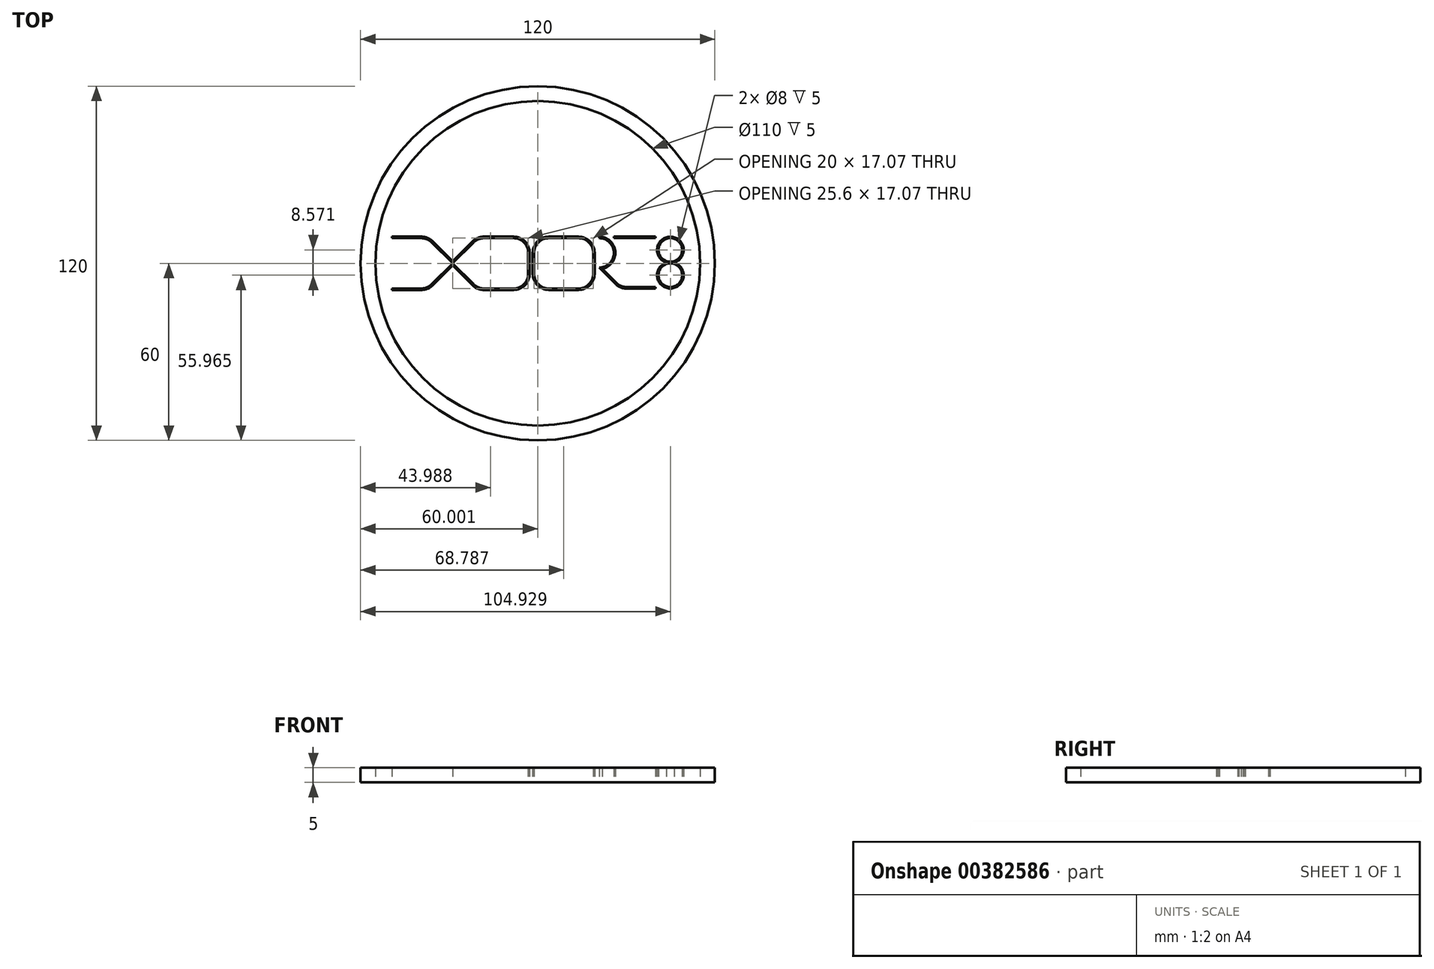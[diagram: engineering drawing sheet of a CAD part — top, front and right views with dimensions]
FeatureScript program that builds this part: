
annotation { "Feature Type Name" : "Feature", "Feature Type Description" : "" }
export const myFeature = defineFeature(function(context is Context, id is Id, definition is map)
    precondition{}
    {
        {
            var Q0;
            Q0=qCreatedBy(makeId("Top.planeOp"),FACE);
            var sketch = newSketch(context, id + "F0", { "sketchPlane" : qUnion([Q0])});
            skLineSegment(sketch, "E0", {"start": v(-7.07, 7.07) * mm, "end": v(0, 0) * mm});
            skLineSegment(sketch, "E1", {"start": v(-7.07, -7.07) * mm, "end": v(0, 0) * mm});
            skLineSegment(sketch, "E2", {"start": v(0, 0) * mm, "end": v(7.07, 7.07) * mm});
            skLineSegment(sketch, "E3", {"start": v(0, 0) * mm, "end": v(7.07, -7.07) * mm});
            skArc(sketch, "E4", {"start": v(-7.07, 7.07) * mm, "mid": v(-8.7, 8.15) * mm, "end": v(-10.6, 8.54) * mm});
            skLineSegment(sketch, "E5", {"start": v(-10.6, 8.54) * mm, "end": v(-20.6, 8.54) * mm});
            skArc(sketch, "E6", {"start": v(-10.6, -8.54) * mm, "mid": v(-8.7, -8.15) * mm, "end": v(-7.07, -7.07) * mm});
            skLineSegment(sketch, "E7", {"start": v(-10.6, -8.54) * mm, "end": v(-20.6, -8.54) * mm});
            skArc(sketch, "E8", {"start": v(10.6, 8.54) * mm, "mid": v(8.7, 8.15) * mm, "end": v(7.07, 7.07) * mm});
            skLineSegment(sketch, "E9", {"start": v(10.6, 8.54) * mm, "end": v(20.6, 8.54) * mm});
            skArc(sketch, "E10", {"start": v(7.07, -7.07) * mm, "mid": v(8.7, -8.15) * mm, "end": v(10.6, -8.54) * mm});
            skLineSegment(sketch, "E11", {"start": v(10.6, -8.54) * mm, "end": v(20.6, -8.54) * mm});
            skArc(sketch, "E12", {"start": v(25.6, 3.54) * mm, "mid": v(24.14, 7.07) * mm, "end": v(20.6, 8.54) * mm});
            skArc(sketch, "E13", {"start": v(20.6, -8.54) * mm, "mid": v(24.14, -7.07) * mm, "end": v(25.6, -3.54) * mm});
            skLineSegment(sketch, "E14", {"start": v(25.6, 3.54) * mm, "end": v(25.6, -3.54) * mm});
            skLineSegment(sketch, "E15", {"start": v(27.6, 3.54) * mm, "end": v(27.6, -3.54) * mm});
            skArc(sketch, "E16", {"start": v(32.6, 8.54) * mm, "mid": v(29.07, 7.07) * mm, "end": v(27.6, 3.54) * mm});
            skArc(sketch, "E17", {"start": v(27.6, -3.54) * mm, "mid": v(29.07, -7.07) * mm, "end": v(32.6, -8.54) * mm});
            skLineSegment(sketch, "E18", {"start": v(32.6, 8.54) * mm, "end": v(42.6, 8.54) * mm});
            skLineSegment(sketch, "E19", {"start": v(32.6, -8.54) * mm, "end": v(42.6, -8.54) * mm});
            skArc(sketch, "E20", {"start": v(47.6, 3.54) * mm, "mid": v(46.14, 7.07) * mm, "end": v(42.6, 8.54) * mm});
            skArc(sketch, "E21", {"start": v(42.6, -8.54) * mm, "mid": v(46.14, -7.07) * mm, "end": v(47.6, -3.54) * mm});
            skLineSegment(sketch, "E22", {"start": v(47.6, -3.54) * mm, "end": v(47.6, 3.54) * mm});
            skArc(sketch, "E23", {"start": v(49.6, -1.46) * mm, "mid": v(54.6, 3.54) * mm, "end": v(49.6, 8.54) * mm});
            skLineSegment(sketch, "E24", {"start": v(49.6, -1.46) * mm, "end": v(55.21, -7.07) * mm});
            skArc(sketch, "E25", {"start": v(55.21, -7.07) * mm, "mid": v(56.84, -8.15) * mm, "end": v(58.75, -8.54) * mm});
            skLineSegment(sketch, "E26", {"start": v(58.75, -8.54) * mm, "end": v(68.75, -8.54) * mm});
            skLineSegment(sketch, "E27", {"start": v(54.6, 8.54) * mm, "end": v(68.75, 8.54) * mm});
            skCircle(sketch, "E28", {"center": v(73.75, 4.54) * mm, "radius": 4 * mm});
            skCircle(sketch, "E29", {"center": v(73.75, -4.04) * mm, "radius": 4.5 * mm});
            skLineSegment(sketch, "E30.0", {"start": v(-10.6, 9.04) * mm, "end": v(-20.6, 9.04) * mm});
            skArc(sketch, "E30.1", {"start": v(-6.72, 7.42) * mm, "mid": v(-8.5, 8.62) * mm, "end": v(-10.6, 9.04) * mm});
            skLineSegment(sketch, "E30.2", {"start": v(-6.72, 7.42) * mm, "end": v(0, 0.7) * mm});
            skArc(sketch, "E30.3", {"start": v(26.1, 3.54) * mm, "mid": v(24.5, 7.42) * mm, "end": v(20.6, 9.04) * mm});
            skLineSegment(sketch, "E30.4", {"start": v(10.6, 9.04) * mm, "end": v(20.6, 9.04) * mm});
            skArc(sketch, "E30.5", {"start": v(10.6, 9.04) * mm, "mid": v(8.5, 8.62) * mm, "end": v(6.72, 7.42) * mm});
            skLineSegment(sketch, "E30.6", {"start": v(0, 0.7) * mm, "end": v(6.72, 7.42) * mm});
            skLineSegment(sketch, "E31.0", {"start": v(26.1, 3.54) * mm, "end": v(26.1, -3.54) * mm});
            skArc(sketch, "E32.0", {"start": v(20.6, -9.04) * mm, "mid": v(24.5, -7.42) * mm, "end": v(26.1, -3.54) * mm});
            skLineSegment(sketch, "E32.1", {"start": v(10.6, -9.04) * mm, "end": v(20.6, -9.04) * mm});
            skArc(sketch, "E32.2", {"start": v(6.72, -7.42) * mm, "mid": v(8.5, -8.62) * mm, "end": v(10.6, -9.04) * mm});
            skLineSegment(sketch, "E32.3", {"start": v(-10.6, -9.04) * mm, "end": v(-20.6, -9.04) * mm});
            skArc(sketch, "E32.4", {"start": v(-10.6, -9.04) * mm, "mid": v(-8.5, -8.62) * mm, "end": v(-6.72, -7.42) * mm});
            skLineSegment(sketch, "E32.5", {"start": v(-6.72, -7.42) * mm, "end": v(0, -0.7) * mm});
            skLineSegment(sketch, "E32.6", {"start": v(0, -0.7) * mm, "end": v(6.72, -7.42) * mm});
            skLineSegment(sketch, "E33.0", {"start": v(32.6, 9.04) * mm, "end": v(42.6, 9.04) * mm});
            skArc(sketch, "E33.1", {"start": v(48.1, 3.54) * mm, "mid": v(46.5, 7.42) * mm, "end": v(42.6, 9.04) * mm});
            skArc(sketch, "E33.2", {"start": v(32.6, 9.04) * mm, "mid": v(28.72, 7.42) * mm, "end": v(27.1, 3.54) * mm});
            skLineSegment(sketch, "E33.3", {"start": v(48.1, -3.54) * mm, "end": v(48.1, 3.54) * mm});
            skLineSegment(sketch, "E33.4", {"start": v(27.1, 3.54) * mm, "end": v(27.1, -3.54) * mm});
            skArc(sketch, "E33.5", {"start": v(27.1, -3.54) * mm, "mid": v(28.72, -7.42) * mm, "end": v(32.6, -9.04) * mm});
            skLineSegment(sketch, "E33.6", {"start": v(32.6, -9.04) * mm, "end": v(42.6, -9.04) * mm});
            skArc(sketch, "E33.7", {"start": v(42.6, -9.04) * mm, "mid": v(46.5, -7.42) * mm, "end": v(48.1, -3.54) * mm});
            skArc(sketch, "E34.0", {"start": v(50.7, -1.85) * mm, "mid": v(55.08, 4.09) * mm, "end": v(49.6, 9.04) * mm});
            skLineSegment(sketch, "E34.1", {"start": v(50.7, -1.85) * mm, "end": v(55.57, -6.72) * mm});
            skArc(sketch, "E34.2", {"start": v(55.57, -6.72) * mm, "mid": v(57.03, -7.7) * mm, "end": v(58.75, -8.04) * mm});
            skLineSegment(sketch, "E34.3", {"start": v(58.75, -8.04) * mm, "end": v(68.75, -8.04) * mm});
            skLineSegment(sketch, "E35.0", {"start": v(54.6, 9.04) * mm, "end": v(68.75, 9.04) * mm});
            skCircle(sketch, "E36.0", {"center": v(73.75, 4.54) * mm, "radius": 4.5 * mm});
            skCircle(sketch, "E37.0", {"center": v(73.75, -4.04) * mm, "radius": 4 * mm});
            skLineSegment(sketch, "E38", {"start": v(54.6, 9.04) * mm, "end": v(54.6, 8.54) * mm});
            skLineSegment(sketch, "E39", {"start": v(68.75, 9.04) * mm, "end": v(68.75, 8.54) * mm});
            skLineSegment(sketch, "E40", {"start": v(68.75, -8.04) * mm, "end": v(68.75, -8.54) * mm});
            skLineSegment(sketch, "E41", {"start": v(49.6, 9.04) * mm, "end": v(49.6, 8.54) * mm});
            skLineSegment(sketch, "E42", {"start": v(-20.6, 9.04) * mm, "end": v(-20.6, 8.54) * mm});
            skLineSegment(sketch, "E43", {"start": v(-20.6, -8.54) * mm, "end": v(-20.6, -9.04) * mm});
            skLineSegment(sketch, "E44", {"start": v(26.1, 3.54) * mm, "end": v(25.6, 3.54) * mm});
            skLineSegment(sketch, "E45", {"start": v(26.1, -3.54) * mm, "end": v(25.6, -3.54) * mm});
            skLineSegment(sketch, "E46", {"start": v(0, 0.7) * mm, "end": v(0, 0) * mm});
            skLineSegment(sketch, "E47", {"start": v(0, 0) * mm, "end": v(0, -0.7) * mm});
            skLineSegment(sketch, "E48", {"start": v(0.01, 0.01) * mm, "end": v(0.01, -0.01) * mm});
            skLineSegment(sketch, "E49", {"start": v(0, 0.01) * mm, "end": v(-0.01, -0.01) * mm});
            skPoint(sketch, "E50", {"position": v(78.25, 4.54) * mm});
            skPoint(sketch, "E51", {"position": v(78.25, -4.04) * mm});
            skPoint(sketch, "E52", {"position": v(28.82, 0) * mm});
            skCircle(sketch, "E53", {"center": v(28.82, 0) * mm, "radius": 55 * mm});
            skCircle(sketch, "E54.0", {"center": v(28.82, 0) * mm, "radius": 60 * mm});
            skArc(sketch, "E55", {"start": v(32.6, -8.54) * mm, "mid": v(34.02, -7.95) * mm, "end": v(34.6, -6.54) * mm});
            skSolve(sketch);
        }
        {
            var Q0;
            Q0=makeQuery(id+"F0.imprint","IMPRINT",FACE,{"disambiguationData":[TD([[makeQuery(id+"F0.imprint","IMPRINT",EDGE,{"derivedFrom":sQuery(id+"F0.wireOp",EDGE,"E23")}),-1.0]])]});
            var Q1;
            Q1=makeQuery(id+"F0.imprint","IMPRINT",FACE,{"disambiguationData":[TD([[makeQuery(id+"F0.imprint","IMPRINT",EDGE,{"derivedFrom":sQuery(id+"F0.wireOp",EDGE,"E27")}),1.0]])]});
            var Q2;
            {var subQ0=sQuery(id+"F0.wireOp",EDGE,"E29");var subQ1=sQuery(id+"F0.wireOp",EDGE,"E28");var subQ2=makeQuery(id+"F0.imprint","INTERSECT",VERTEX,{"disambiguationData":[OD(0.0)],"derivedFrom":[subQ1,subQ0]});Q2=makeQuery(id+"F0.imprint","IMPRINT",FACE,{"disambiguationData":[TD([[makeQuery(id+"F0.imprint","IMPRINT",EDGE,{"disambiguationData":[TD([[subQ2,1.0]])],"derivedFrom":subQ1}),-1.0]])]});}
            var Q3;
            {var subQ0=sQuery(id+"F0.wireOp",EDGE,"E36.0");var subQ1=sQuery(id+"F0.wireOp",EDGE,"E29");var subQ2=makeQuery(id+"F0.imprint","INTERSECT",VERTEX,{"disambiguationData":[OD(0.0)],"derivedFrom":[subQ1,subQ0]});Q3=makeQuery(id+"F0.imprint","IMPRINT",FACE,{"disambiguationData":[TD([[makeQuery(id+"F0.imprint","IMPRINT",EDGE,{"disambiguationData":[TD([[subQ2,1.0]])],"derivedFrom":subQ1}),1.0]])]});}
            var Q4;
            Q4=makeQuery(id+"F0.imprint","IMPRINT",FACE,{"disambiguationData":[TD([[makeQuery(id+"F0.imprint","IMPRINT",EDGE,{"derivedFrom":sQuery(id+"F0.wireOp",EDGE,"E15")}),-1.0]])]});
            var Q5;
            Q5=makeQuery(id+"F0.imprint","IMPRINT",FACE,{"disambiguationData":[TD([[makeQuery(id+"F0.imprint","IMPRINT",EDGE,{"derivedFrom":sQuery(id+"F0.wireOp",EDGE,"E0")}),1.0]])]});
            var Q6;
            Q6=makeQuery(id+"F0.imprint","IMPRINT",FACE,{"disambiguationData":[TD([[makeQuery(id+"F0.imprint","IMPRINT",EDGE,{"derivedFrom":sQuery(id+"F0.wireOp",EDGE,"E2")}),1.0]])]});
            var Q7;
            Q7=makeQuery(id+"F0.imprint","IMPRINT",FACE,{"disambiguationData":[TD([[makeQuery(id+"F0.imprint","IMPRINT",EDGE,{"derivedFrom":sQuery(id+"F0.wireOp",EDGE,"E14")}),1.0]])]});
            var Q8;
            Q8=makeQuery(id+"F0.imprint","IMPRINT",FACE,{"disambiguationData":[TD([[makeQuery(id+"F0.imprint","IMPRINT",EDGE,{"derivedFrom":sQuery(id+"F0.wireOp",EDGE,"E1")}),-1.0]])]});
            var Q9;
            {var subQ0=sQuery(id+"F0.wireOp",EDGE,"E10");Q9=makeQuery(id+"F0.imprint","IMPRINT",FACE,{"disambiguationData":[TD([[makeQuery(id+"F0.imprint","IMPRINT",EDGE,{"derivedFrom":subQ0}),-1.0]])]});}
            var Q10;
            {var subQ3=sQuery(id+"F0.wireOp",EDGE,"E48");Q10=makeQuery(id+"F0.imprint","IMPRINT",FACE,{"disambiguationData":[TD([[makeQuery(id+"F0.imprint","IMPRINT",EDGE,{"derivedFrom":subQ3}),-1.0]])]});}
            var Q11;
            {var subQ3=sQuery(id+"F0.wireOp",EDGE,"E49");Q11=makeQuery(id+"F0.imprint","IMPRINT",FACE,{"disambiguationData":[TD([[makeQuery(id+"F0.imprint","IMPRINT",EDGE,{"derivedFrom":subQ3}),1.0]])]});}
            var Q12;
            Q12=makeQuery(id+"F0.imprint","IMPRINT",FACE,{"disambiguationData":[TD([[makeQuery(id+"F0.imprint","IMPRINT",EDGE,{"derivedFrom":sQuery(id+"F0.wireOp",EDGE,"E37.0")}),-1.0]])]});
            var Q13;
            Q13=makeQuery(id+"F0.imprint","IMPRINT",FACE,{"disambiguationData":[TD([[makeQuery(id+"F0.imprint","IMPRINT",EDGE,{"derivedFrom":sQuery(id+"F0.wireOp",EDGE,"E53")}),-1.0]])]});
            extrude(context, id + "F1", {"entities" : qUnion([Q0, Q1, Q2, Q3, Q4, Q5, Q6, Q7, Q8, Q9, Q10, Q11, Q12, Q13]), "depth" : 5 * mm});
        }
    });
